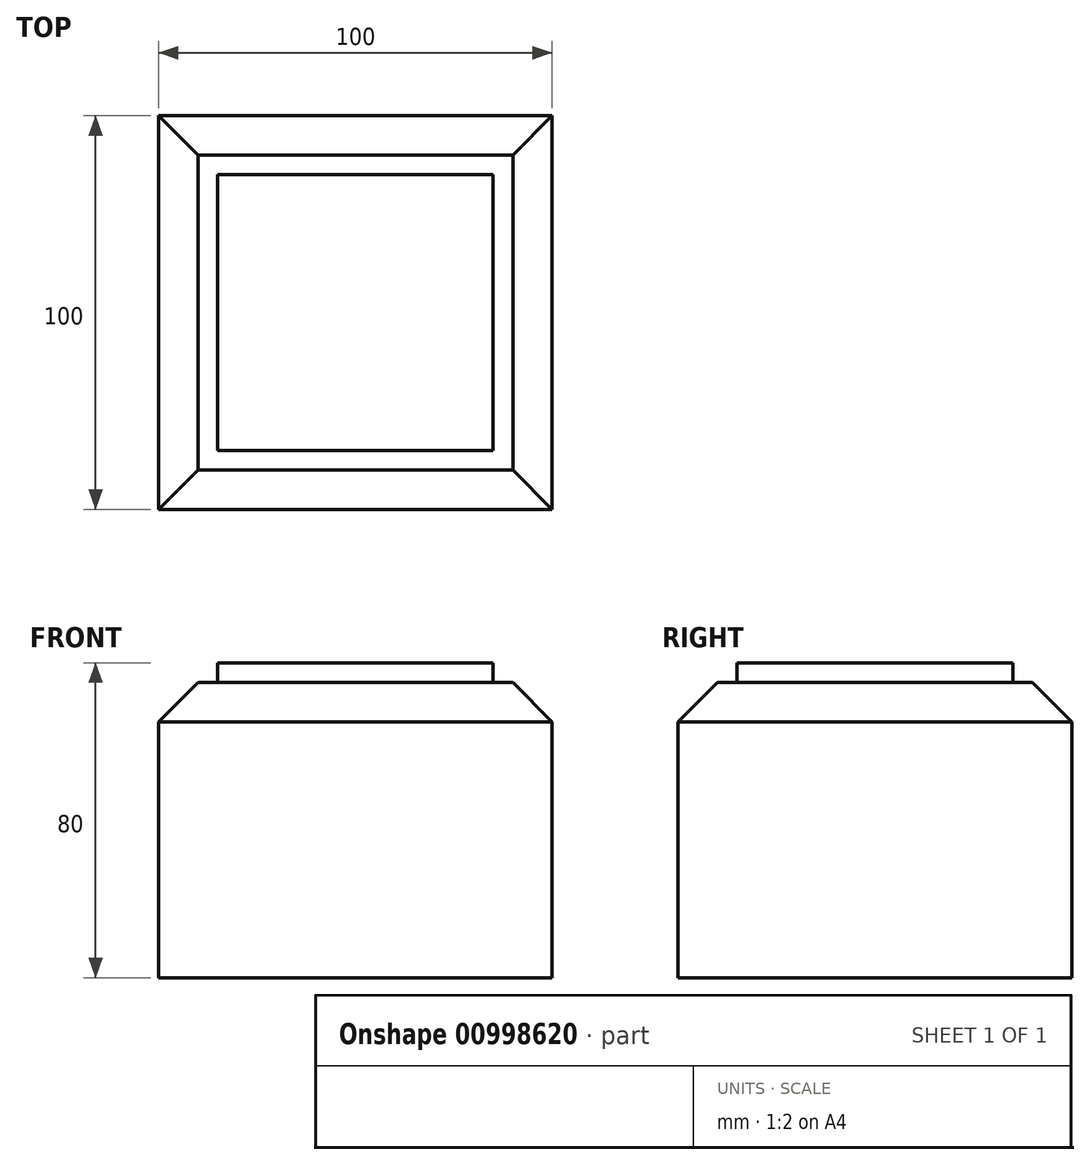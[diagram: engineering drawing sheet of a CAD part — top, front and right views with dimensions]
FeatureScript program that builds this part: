
annotation { "Feature Type Name" : "Feature", "Feature Type Description" : "" }
export const myFeature = defineFeature(function(context is Context, id is Id, definition is map)
    precondition{}
    {
        {
            var Q0;
            Q0=qCreatedBy(makeId("Top.planeOp"),FACE);
            var sketch = newSketch(context, id + "F0", { "sketchPlane" : qUnion([Q0])});
            skLineSegment(sketch, "E0.bottom", {"start": v(-51.7, 50.15) * mm, "end": v(48.3, 50.15) * mm});
            skLineSegment(sketch, "E0.top", {"start": v(-51.7, -49.85) * mm, "end": v(48.3, -49.85) * mm});
            skLineSegment(sketch, "E0.left", {"start": v(-51.7, 50.15) * mm, "end": v(-51.7, -49.85) * mm});
            skLineSegment(sketch, "E0.right", {"start": v(48.3, 50.15) * mm, "end": v(48.3, -49.85) * mm});
            skSolve(sketch);
        }
        {
            var Q0;
            Q0=makeQuery(id+"F0.imprint","IMPRINT",FACE,{"disambiguationData":[TD([[makeQuery(id+"F0.imprint","IMPRINT",EDGE,{"derivedFrom":sQuery(id+"F0.wireOp",EDGE,"E0.bottom")}),-1.0]])]});
            extrude(context, id + "F1", {"entities" : qUnion([Q0]), "depth" : 75 * mm, "offsetDistance" : 25 * mm});
        }
        {
            var Q0;
            Q0=makeQuery(id+"F1.opExtrude","CAP_EDGE",EDGE,{"disambiguationData":[OSD([sQuery(id+"F0.wireOp",EDGE,"E0.left")])],"isStart":false});
            var Q1;
            Q1=makeQuery(id+"F1.opExtrude","CAP_EDGE",EDGE,{"disambiguationData":[OSD([sQuery(id+"F0.wireOp",EDGE,"E0.top")])],"isStart":false});
            var Q2;
            Q2=makeQuery(id+"F1.opExtrude","CAP_EDGE",EDGE,{"disambiguationData":[OSD([sQuery(id+"F0.wireOp",EDGE,"E0.bottom")])],"isStart":false});
            var Q3;
            Q3=makeQuery(id+"F1.opExtrude","CAP_EDGE",EDGE,{"disambiguationData":[OSD([sQuery(id+"F0.wireOp",EDGE,"E0.right")])],"isStart":false});
            chamfer(context, id + "F2", {"entities" : qUnion([Q0, Q1, Q2, Q3]), "width" : 10 * mm, "tangentPropagation" : true});
        }
        {
            var Q0;
            Q0=makeQuery(id+"F1.opExtrude","CAP_FACE",FACE,{"disambiguationData":[OSD([sQuery(id+"F0.wireOp",EDGE,"E0.bottom"),sQuery(id+"F0.wireOp",EDGE,"E0.top"),sQuery(id+"F0.wireOp",EDGE,"E0.left"),sQuery(id+"F0.wireOp",EDGE,"E0.right")])],"isStart":false});
            var sketch = newSketch(context, id + "F3", { "sketchPlane" : qUnion([Q0])});
            skLineSegment(sketch, "E1.0", {"start": v(33.3, -34.85) * mm, "end": v(33.3, 40.15) * mm});
            skLineSegment(sketch, "E1.1", {"start": v(-36.7, -34.85) * mm, "end": v(33.3, -34.85) * mm});
            skLineSegment(sketch, "E1.2", {"start": v(-36.7, 40.15) * mm, "end": v(-36.7, -34.85) * mm});
            skLineSegment(sketch, "E2.0", {"start": v(38.3, 35.15) * mm, "end": v(-41.7, 35.15) * mm});
            skSolve(sketch);
        }
        {
            var Q0;
            {var subQ0=sQuery(id+"F3.wireOp",EDGE,"E1.1");Q0=makeQuery(id+"F3.imprint","IMPRINT",FACE,{"disambiguationData":[TD([[makeQuery(id+"F3.imprint","IMPRINT",EDGE,{"derivedFrom":subQ0}),1.0]])]});}
            var sketch = newSketch(context, id + "F4", { "sketchPlane" : qUnion([Q0])});
            skSolve(sketch);
        }
        {
            var Q0;
            {var subQ0=sQuery(id+"F3.wireOp",EDGE,"E1.1");Q0=makeQuery(id+"F4.imprint","IMPRINT",FACE,{"disambiguationData":[TD([[makeQuery(id+"F4.imprint","IMPRINT",EDGE,{"derivedFrom":makeQuery(id+"F3.imprint","IMPRINT",EDGE,{"derivedFrom":subQ0})}),1.0]])]});}
            extrude(context, id + "F5", {"entities" : qUnion([Q0]), "operationType" : NewBodyOperationType.ADD, "depth" : 5 * mm, "offsetDistance" : 25 * mm});
        }
    });
